# Revit family: FP_Revit_18_EB30PSX1_Coffee_Maker_90001972A
name_source: partatom
category: Specialty Equipment
revit_build: Autodesk Revit 2018 (Build: 20170223_1515(x64)
units: mm (PartAtom-declared; Revit-internal decimal feet)

## family parameters
Always vertical = Yes
Cut with Voids When Loaded = Yes
OmniClass Number = 23.40.40.14.17.31
OmniClass Title = Small Specialized Cooking Equipment
Part Type = Normal
Room Calculation Point = No
Round Connector Dimension = Use Diameter
Shared = No
Work Plane-Based = No

## types (1)
- EB30PSX1
    Cavity - Depth = 560 mm  [stored 1.83727 ft]
    Cavity - Height = 474 mm  [stored 1.55512 ft]
    Cavity - Width = 762 mm  [stored 2.5 ft]
    Chassis - Depth = 445 mm  [stored 1.45997 ft]
    Chassis - Height = 457 mm  [stored 1.49934 ft]
    Chassis - Width = 560 mm  [stored 1.83727 ft]
    Connector Description - Electrical = 120 V, 60 Hz, 11.25 A
    Description = 30" Built in Coffee Maker
    Manufacturer = Fisher & Paykel Appliances
    Material - Body = Fisher & Paykel - Glass, Black
    Material - Display Panel = Fisher & Paykel - Glass, Black
    Material - Logo = Fisher & Paykel - Steel, Chrome Plated
    Material - Trim = Fisher & Paykel - Stainless Steel
    Model = EB30PSX1
    Product - Depth = 484 mm  [stored 1.58793 ft]
    Product - Height = 470 mm  [stored 1.54199 ft]
    Product - Width = 757 mm
    URL = www.fisherpaykel.com
    Visibility - Clearance Required = Yes

note: [stored X ft] marks values corroborated as IEEE doubles in the binary element streams (Revit-internal decimal feet)

## geometry (parser evidence)
native form markers: Sweep x1
no freeform markers — native parametric forms only
